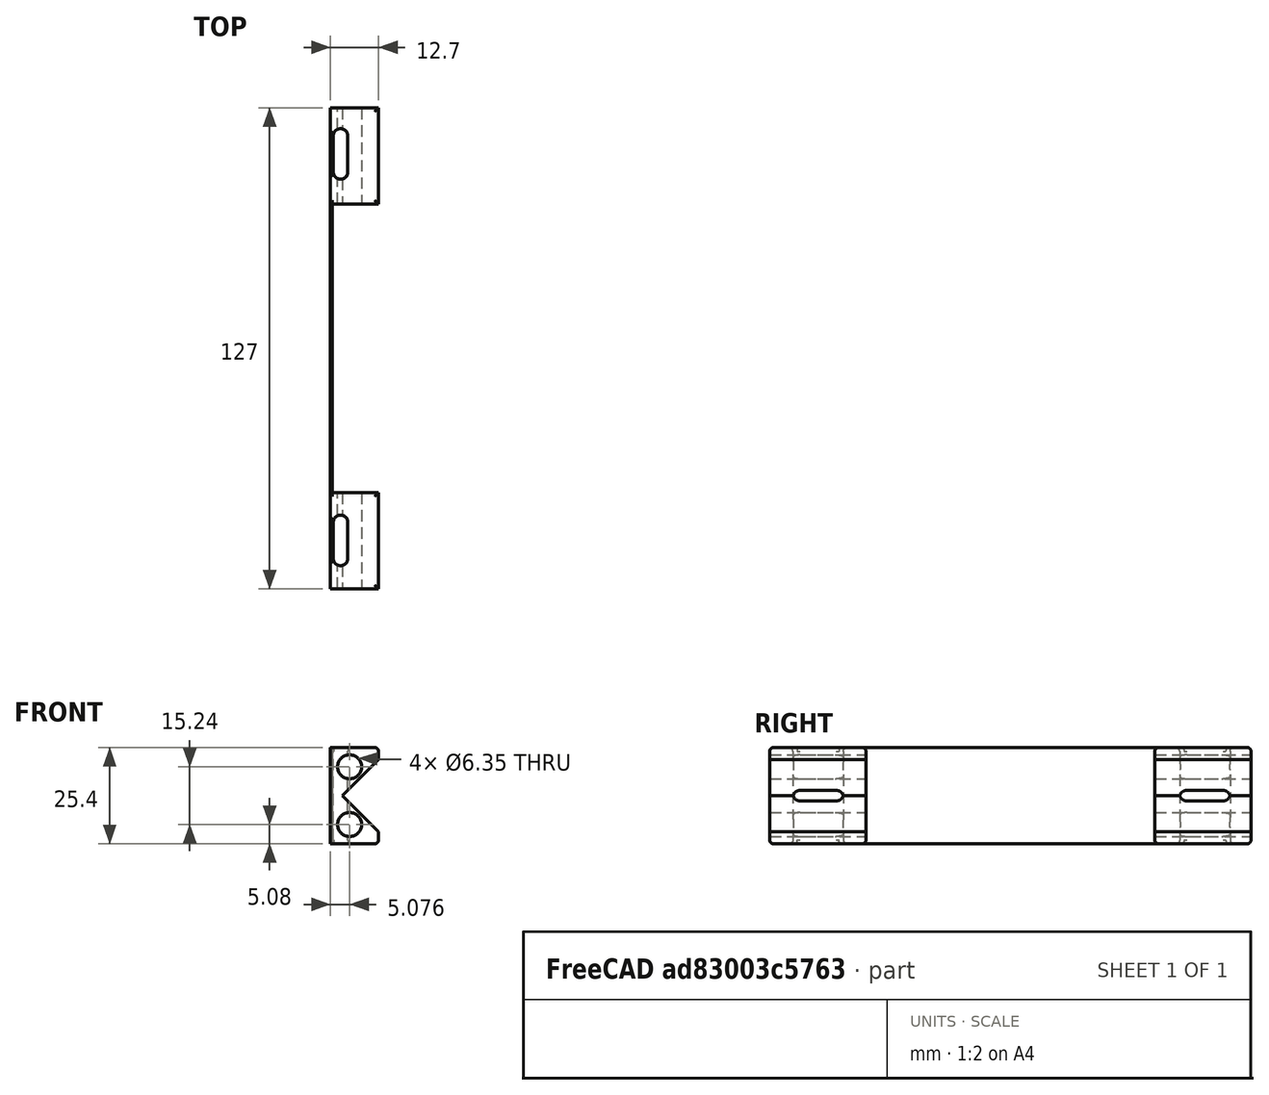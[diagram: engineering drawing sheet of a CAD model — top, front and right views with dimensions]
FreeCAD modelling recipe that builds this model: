
FCSTD DOCUMENT  (FreeCAD 0.19R24291 (Git))
Label: BackPanel_Hanging
License: All rights reserved
LicenseURL: http://en.wikipedia.org/wiki/All_rights_reserved
objects: PartDesign::Fillet×8, Sketcher::SketchObject×3, PartDesign::Pocket×2, Mesh::Feature×1, PartDesign::Pad×1, PartDesign::Body×1, Part::Feature×1, Part::Compound×1
note: 28 computed .brp shape members not serialized (recipe doc carries the construction recipe); baked Part::Feature solids carry a one-line shape summary decoded from their .brp

FEATURE [Mesh::Feature] U_Box_V104_General_Alarm_Device_Backpanel
  Placement = pos=(0,0,0.237998) rot=(0,0,1;0rad)
FEATURE [Sketcher::SketchObject] Sketch
  FullyConstrained = false
  MapMode = 5
  Placement = pos=(0,0,0) rot=(1,0,0;1.5708rad)
  Support = -> [XZ_Plane]
  sketch-geometry (10):
    g0: LineSegment StartX=4.66087 StartY=33.0204 StartZ=0 EndX=4.66087 EndY=7.62039 EndZ=0
    g1: LineSegment StartX=4.66087 StartY=7.62039 StartZ=0 EndX=17.3609 EndY=7.62039 EndZ=0
    g2: LineSegment StartX=17.3609 StartY=10.7954 StartZ=0 EndX=7.83587 EndY=20.3204 EndZ=0
    g3: LineSegment StartX=7.83587 StartY=20.3204 StartZ=0 EndX=17.3609 EndY=29.8454 EndZ=0
    g4: LineSegment StartX=17.3609 StartY=33.0204 StartZ=0 EndX=4.66087 EndY=33.0204 EndZ=0
    g5: LineSegment StartX=17.3609 StartY=33.0204 StartZ=0 EndX=17.3609 EndY=29.8454 EndZ=0
    g6: LineSegment StartX=17.3609 StartY=10.7954 StartZ=0 EndX=17.3609 EndY=7.62039 EndZ=0
    g7: Circle CenterX=9.74087 CenterY=27.9404 CenterZ=0 NormalX=0 NormalY=0 NormalZ=1 AngleXU=0 Radius=3.175
    g8: Circle CenterX=9.74087 CenterY=12.7004 CenterZ=0 NormalX=0 NormalY=0 NormalZ=1 AngleXU=0 Radius=3.175
    g9: LineSegment StartX=7.83587 StartY=20.3204 StartZ=0 EndX=25.4001 EndY=20.3204 EndZ=0
  constraints (25):
    c: Vertical(g0)
    c: Coincident(g0,g1)
    c: Horizontal(g1)
    c: Coincident(g2,g3)
    c: Coincident(g4,g0)
    c: Horizontal(g4)
    c: Equal(g4,g1)
    c: DistanceX(g4,g4) = 12.7
    c: Angle(g4,g3) = 0.785398
    c: Angle(g2,g1) = 0.785398
    c: Vertical(g2,g1)
    c: Vertical(g3,g4)
    c: Coincident(g4,g5)
    c: Coincident(g5,g3)
    c: Coincident(g2,g6)
    c: Coincident(g6,g1)
    c: DistanceX(g0,g2) = 3.175
    c: Equal(g5,g6)
    c: DistanceY(g0,g0) = 25.4
    c: Radius(g7) = 3.175
    c: Equal(g7,g8) = 3.429
    c: Vertical(g7,g8)
    c: DistanceX(g0,g7) = 5.08
    c: Coincident(g9,g2)
    c: Symmetric(g7,g8,g9)
FEATURE [PartDesign::Pad] Pad
  Direction = (0,6,0)
  Length = 127
  Length2 = 99.9998
  Placement = pos=(0,0,0) rot=(1,0,0;1.5708rad)
  Profile = -> Sketch
  Type = 0
FEATURE [Sketcher::SketchObject] Sketch001
  FullyConstrained = false
  MapMode = 5
  Support = -> [XY_Plane]
  sketch-geometry (4):
    g0: LineSegment StartX=25.4 StartY=-101.6 StartZ=0 EndX=5.21051 EndY=-101.6 EndZ=0
    g1: LineSegment StartX=5.21051 StartY=-101.6 StartZ=0 EndX=5.21051 EndY=-25.4 EndZ=0
    g2: LineSegment StartX=5.21051 StartY=-25.4 StartZ=0 EndX=25.4 EndY=-25.4 EndZ=0
    g3: LineSegment StartX=25.4 StartY=-25.4 StartZ=0 EndX=25.4 EndY=-101.6 EndZ=0
  constraints (9):
    c: Coincident(g0,g1)
    c: Coincident(g1,g2)
    c: Coincident(g2,g3)
    c: Coincident(g3,g0)
    c: Horizontal(g0)
    c: Horizontal(g2)
    c: Vertical(g1)
    c: Vertical(g3)
    c: DistanceY(g3,g3) = 76.2
FEATURE [PartDesign::Pocket] Pocket
  BaseFeature = -> Pad
  Length = 5.0038
  Length2 = 99.9998
  Midplane = true
  Placement = pos=(0,0,0) rot=(1,0,0;1.5708rad)
  Profile = -> Sketch001
  Reversed = true
  Type = 1
FEATURE [Sketcher::SketchObject] Sketch002
  FullyConstrained = false
  MapMode = 5
  Support = -> [XY_Plane]
  sketch-geometry (8):
    g0: ArcOfCircle CenterX=7.3341 CenterY=-7.40419 CenterZ=0 NormalX=0 NormalY=0 NormalZ=1 AngleXU=0 Radius=1.905 StartAngle=2e-16 EndAngle=3.14159
    g1: ArcOfCircle CenterX=7.3341 CenterY=-16.9292 CenterZ=0 NormalX=0 NormalY=0 NormalZ=1 AngleXU=0 Radius=1.905 StartAngle=3.14159 EndAngle=6.28319
    g2: LineSegment StartX=5.4291 StartY=-7.40419 StartZ=0 EndX=5.4291 EndY=-16.9292 EndZ=0
    g3: LineSegment StartX=9.2391 StartY=-7.40419 StartZ=0 EndX=9.2391 EndY=-16.9292 EndZ=0
    g4: ArcOfCircle CenterX=7.3341 CenterY=-109.449 CenterZ=0 NormalX=0 NormalY=0 NormalZ=1 AngleXU=0 Radius=1.905 StartAngle=-9e-16 EndAngle=3.14159
    g5: ArcOfCircle CenterX=7.3341 CenterY=-118.974 CenterZ=0 NormalX=0 NormalY=0 NormalZ=1 AngleXU=0 Radius=1.905 StartAngle=3.14159 EndAngle=6.28319
    g6: LineSegment StartX=5.4291 StartY=-109.449 StartZ=0 EndX=5.4291 EndY=-118.974 EndZ=0
    g7: LineSegment StartX=9.2391 StartY=-109.449 StartZ=0 EndX=9.2391 EndY=-118.974 EndZ=0
  constraints (17):
    c: Tangent(g0,g3) = 1.5708
    c: Tangent(g0,g2) = -1.5708
    c: Tangent(g2,g1) = -1.5708
    c: Tangent(g3,g1) = 1.5708
    c: Vertical(g2)
    c: Equal(g0,g1)
    c: DistanceX(g0,g0) = 3.81
    c: DistanceY(g1,g0) = 9.525
    c: Tangent(g4,g7) = 1.5708
    c: Tangent(g4,g6) = -1.5708
    c: Tangent(g6,g5) = -1.5708
    c: Tangent(g7,g5) = 1.5708
    c: Vertical(g6)
    c: Equal(g4,g5)
    c: Equal(g0,g4) = 3.81
    c: DistanceY(g5,g4) = 9.525
    c: Vertical(g0,g4)
FEATURE [PartDesign::Pocket] Pocket001
  BaseFeature = -> Pocket
  Length = 5.0038
  Length2 = 99.9998
  Placement = pos=(0,0,0) rot=(1,0,0;1.5708rad)
  Profile = -> Sketch002
  Reversed = true
  Type = 1
FEATURE [PartDesign::Fillet] Fillet
  Base = -> Pocket001 [Edge75]
  BaseFeature = -> Pocket001
  Placement = pos=(0,0,0) rot=(1,0,0;1.5708rad)
  Radius = 0.999998
  Refine = true
  SupportTransform = false
FEATURE [PartDesign::Fillet] Fillet001
  Base = -> Fillet [Edge20]
  BaseFeature = -> Fillet
  Placement = pos=(0,0,0) rot=(1,0,0;1.5708rad)
  Radius = 0.999998
  Refine = true
  SupportTransform = false
FEATURE [PartDesign::Fillet] Fillet002
  Base = -> Fillet001 [Edge61]
  BaseFeature = -> Fillet001
  Placement = pos=(0,0,0) rot=(1,0,0;1.5708rad)
  Radius = 0.999998
  Refine = true
  SupportTransform = false
FEATURE [PartDesign::Fillet] Fillet003
  Base = -> Fillet002 [Edge29]
  BaseFeature = -> Fillet002
  Placement = pos=(0,0,0) rot=(1,0,0;1.5708rad)
  Radius = 0.999998
  Refine = true
  SupportTransform = false
FEATURE [PartDesign::Fillet] Fillet004
  Base = -> Fillet003 [Edge24,Edge22,Edge26]
  BaseFeature = -> Fillet003
  Placement = pos=(0,0,0) rot=(1,0,0;1.5708rad)
  Radius = 0.999998
  SupportTransform = false
FEATURE [PartDesign::Fillet] Fillet005
  Base = -> Fillet004 [Edge31,Edge33,Edge35]
  BaseFeature = -> Fillet004
  Placement = pos=(0,0,0) rot=(1,0,0;1.5708rad)
  Radius = 0.999998
  SupportTransform = false
FEATURE [PartDesign::Fillet] Fillet006
  Base = -> Fillet005 [Edge43,Edge59,Edge61]
  BaseFeature = -> Fillet005
  Placement = pos=(0,0,0) rot=(1,0,0;1.5708rad)
  Radius = 0.999998
  SupportTransform = false
FEATURE [PartDesign::Fillet] Fillet007
  Base = -> Fillet006 [Edge44,Edge46,Edge48]
  BaseFeature = -> Fillet006
  Placement = pos=(0,0,0) rot=(1,0,0;1.5708rad)
  Radius = 0.999998
  Refine = true
  SupportTransform = false
FEATURE [PartDesign::Body] Body  label="HangingEars"
  Group = -> [Sketch,Pad,Sketch001,Pocket,Sketch002,Pocket001,Fillet,Fillet001,Fillet002,Fillet003,Fillet004,Fillet005,Fillet006,Fillet007]
  Origin = -> Origin
  Placement = pos=(-0.635,139,0) rot=(0,0,1;0rad)
  Tip = -> Fillet007
FEATURE [Part::Feature] U_Box_V104_General_Alarm_Device_Backpanel001
  shape: bbox 2 x 146.1 x 35.1 mm, 412 faces, 0 solids (baked)
FEATURE [Part::Compound] Compound
  Links = -> [U_Box_V104_General_Alarm_Device_Backpanel001,Body]
